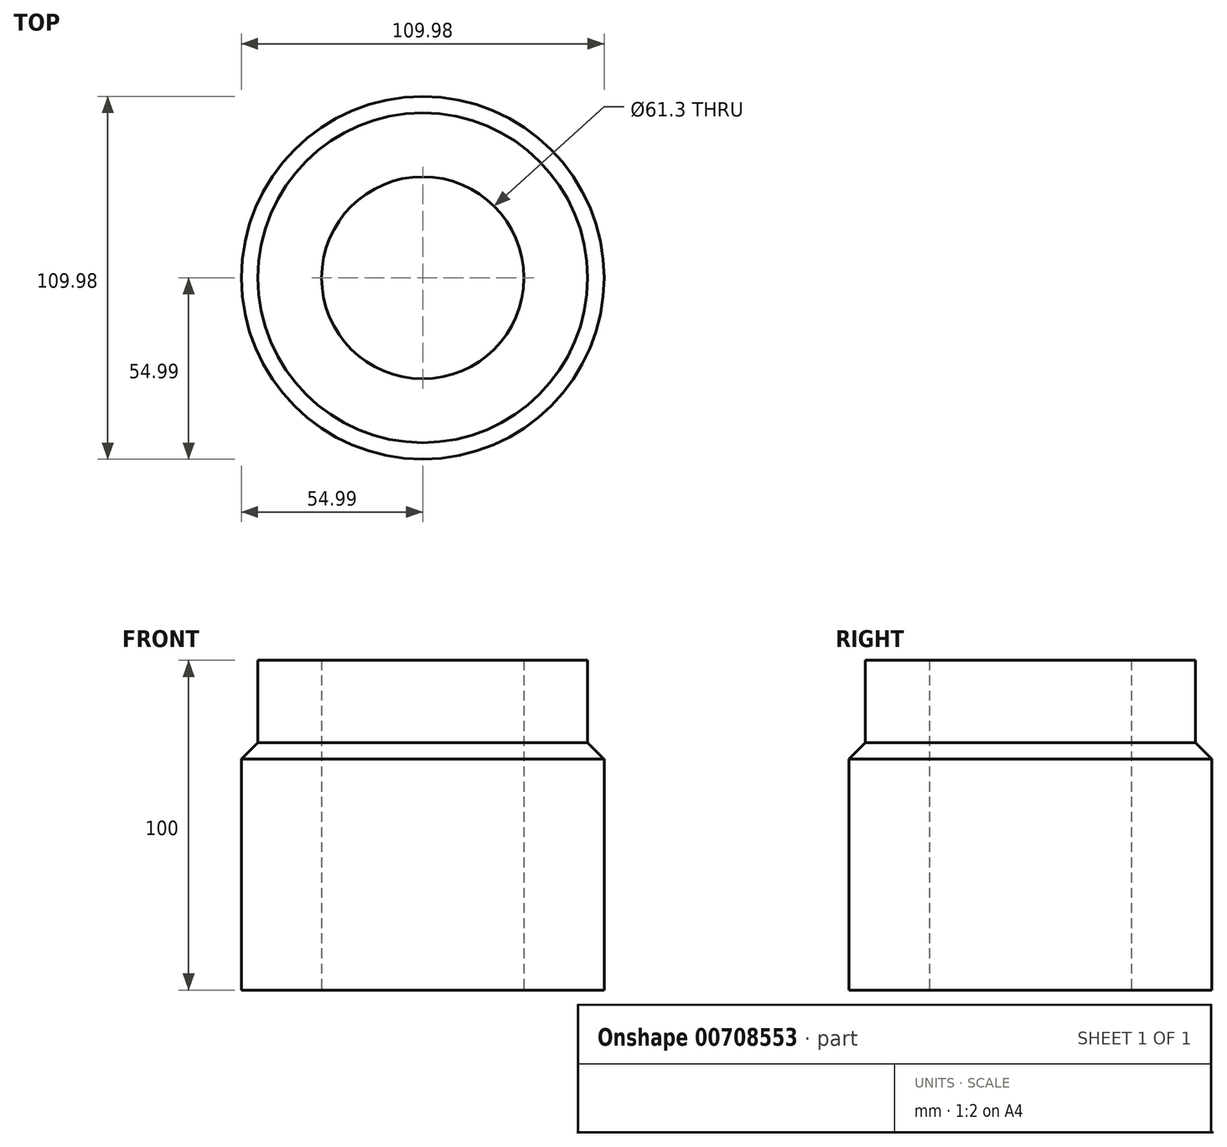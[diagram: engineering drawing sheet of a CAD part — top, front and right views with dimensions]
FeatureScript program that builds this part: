
annotation { "Feature Type Name" : "Feature", "Feature Type Description" : "" }
export const myFeature = defineFeature(function(context is Context, id is Id, definition is map)
    precondition{}
    {
        {
            var Q0;
            Q0=qCreatedBy(makeId("Top.planeOp"),FACE);
            var sketch = newSketch(context, id + "F0", { "sketchPlane" : qUnion([Q0])});
            skCircle(sketch, "E0", {"center": v(0, 0) * mm, "radius": 54.99 * mm});
            skCircle(sketch, "E1", {"center": v(0, 0) * mm, "radius": 30.65 * mm});
            skSolve(sketch);
        }
        {
            var Q0;
            Q0=makeQuery(id+"F0.imprint","IMPRINT",FACE,{"disambiguationData":[TD([[makeQuery(id+"F0.imprint","IMPRINT",EDGE,{"derivedFrom":sQuery(id+"F0.wireOp",EDGE,"E0")}),1.0]])]});
            extrude(context, id + "F1", {"entities" : qUnion([Q0]), "depth" : 25 * mm, "offsetDistance" : 25 * mm});
        }
        {
            var Q0;
            Q0=makeQuery(id+"F1.opExtrude","CAP_FACE",FACE,{"disambiguationData":[OSD([sQuery(id+"F0.wireOp",EDGE,"E0"),sQuery(id+"F0.wireOp",EDGE,"E1")])],"isStart":false});
            extrude(context, id + "F2", {"entities" : qUnion([Q0]), "operationType" : NewBodyOperationType.ADD, "depth" : 50 * mm, "offsetDistance" : 25 * mm});
        }
        {
            var Q0;
            Q0=makeQuery(id+"F2.opExtrude","CAP_EDGE",EDGE,{"disambiguationData":[OSD([sQuery(id+"F0.wireOp",EDGE,"E0")])],"isStart":false});
            chamfer(context, id + "F3", {"entities" : qUnion([Q0]), "width" : 5 * mm, "tangentPropagation" : true});
        }
        {
            var Q0;
            Q0=makeQuery(id+"F2.opExtrude","CAP_FACE",FACE,{"disambiguationData":[OSD([sQuery(id+"F0.wireOp",EDGE,"E0"),sQuery(id+"F0.wireOp",EDGE,"E1")])],"isStart":false});
            extrude(context, id + "F4", {"entities" : qUnion([Q0]), "operationType" : NewBodyOperationType.ADD, "depth" : 25 * mm, "offsetDistance" : 25 * mm});
        }
    });
